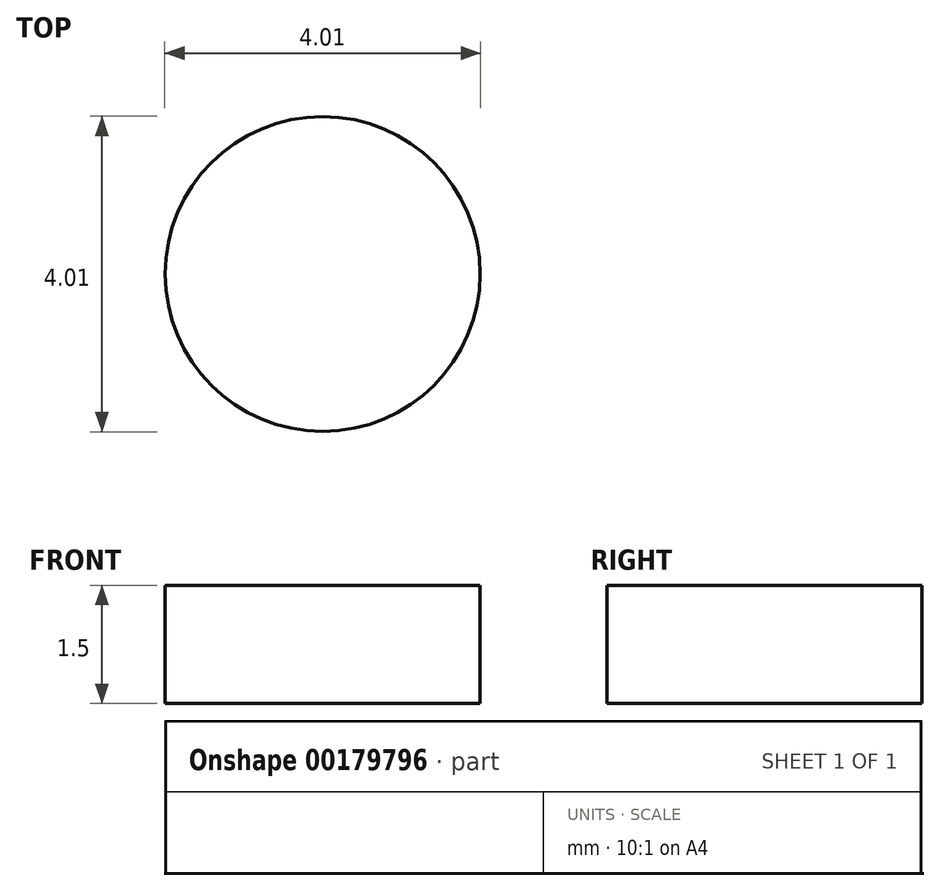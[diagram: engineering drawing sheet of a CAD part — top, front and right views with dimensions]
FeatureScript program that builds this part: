
annotation { "Feature Type Name" : "Feature", "Feature Type Description" : "" }
export const myFeature = defineFeature(function(context is Context, id is Id, definition is map)
    precondition{}
    {
        {
            var Q0;
            Q0=qCreatedBy(makeId("Front.planeOp"),FACE);
            var sketch = newSketch(context, id + "F0", { "sketchPlane" : qUnion([Q0])});
            skLineSegment(sketch, "E0", {"start": v(0, 20) * mm, "end": v(0, 0) * mm});
            skLineSegment(sketch, "E1", {"start": v(0, 0) * mm, "end": v(20, 0) * mm});
            skLineSegment(sketch, "E2", {"start": v(20, 0) * mm, "end": v(20, 1.5) * mm});
            skLineSegment(sketch, "E3", {"start": v(20, 1.5) * mm, "end": v(1.75, 1.5) * mm});
            skLineSegment(sketch, "E4", {"start": v(1.5, 1.75) * mm, "end": v(1.5, 20) * mm});
            skLineSegment(sketch, "E5", {"start": v(1.5, 20) * mm, "end": v(0, 20) * mm});
            skPoint(sketch, "E6.visualSharp", {"position": v(1.5, 1.5) * mm});
            skArc(sketch, "E6.filletArc", {"start": v(1.5, 1.75) * mm, "mid": v(1.57, 1.57) * mm, "end": v(1.75, 1.5) * mm});
            skSolve(sketch);
        }
        {
            var Q0;
            Q0 = qSketchRegion(id + "F0", true);
            extrude(context, id + "F1", {"entities" : qUnion([Q0]), "endBound" : BoundingType.SYMMETRIC, "depth" : 38.1 * mm});
        }
        {
            var Q0;
            Q0=makeQuery(id+"F1.opExtrude","SWEPT_FACE",FACE,{"disambiguationData":[OSD([sQuery(id+"F0.wireOp",EDGE,"E0")])]});
            var sketch = newSketch(context, id + "F2", { "sketchPlane" : qUnion([Q0])});
            skCircle(sketch, "E7", {"center": v(9.53, 8.57) * mm, "radius": 3.18 * mm});
            skCircle(sketch, "E8", {"center": v(-9.53, 5.72) * mm, "radius": 2 * mm});
            skSolve(sketch);
        }
        {
            var Q0;
            Q0 = qSketchRegion(id + "F2", true);
            extrude(context, id + "F3", {"entities" : qUnion([Q0]), "operationType" : NewBodyOperationType.REMOVE, "endBound" : BoundingType.UP_TO_NEXT, "oppositeDirection" : true, "depth" : 25.4 * mm});
        }
        {
            var Q0;
            Q0=makeQuery(id+"F1.opExtrude","SWEPT_FACE",FACE,{"disambiguationData":[OSD([sQuery(id+"F0.wireOp",EDGE,"E1")])]});
            var sketch = newSketch(context, id + "F4", { "sketchPlane" : qUnion([Q0])});
            skCircle(sketch, "E9", {"center": v(8.57, 9.53) * mm, "radius": 3.18 * mm});
            skCircle(sketch, "E10.MirrorC", {"center": v(5.72, -9.53) * mm, "radius": 2 * mm});
            skSolve(sketch);
        }
        {
            var Q0;
            Q0=makeQuery(id+"F4.imprint","IMPRINT",FACE,{"disambiguationData":[TD([[makeQuery(id+"F4.imprint","IMPRINT",EDGE,{"derivedFrom":sQuery(id+"F4.wireOp",EDGE,"E9")}),1.0]])]});
            var Q1;
            Q1=makeQuery(id+"F4.imprint","IMPRINT",FACE,{"disambiguationData":[TD([[makeQuery(id+"F4.imprint","IMPRINT",EDGE,{"derivedFrom":sQuery(id+"F4.wireOp",EDGE,"E10.MirrorC")}),-1.0]])]});
            extrude(context, id + "F5", {"entities" : qUnion([Q0, Q1]), "operationType" : NewBodyOperationType.REMOVE, "endBound" : BoundingType.UP_TO_NEXT, "oppositeDirection" : true, "depth" : 25.4 * mm});
        }
    });
